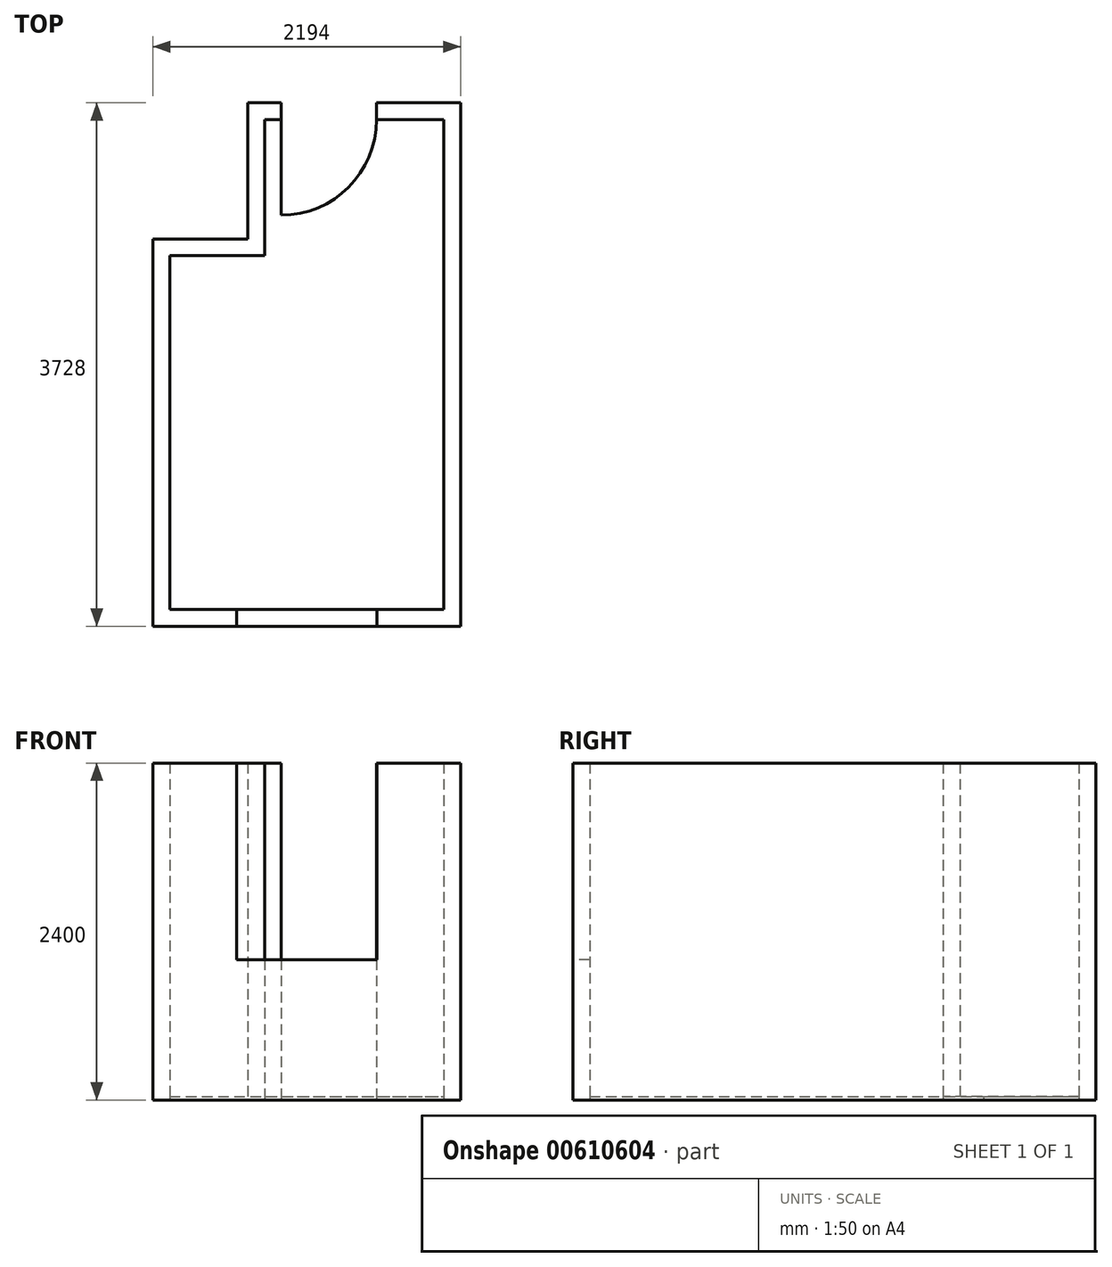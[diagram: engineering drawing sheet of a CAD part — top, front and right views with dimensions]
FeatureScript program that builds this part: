
annotation { "Feature Type Name" : "Feature", "Feature Type Description" : "" }
export const myFeature = defineFeature(function(context is Context, id is Id, definition is map)
    precondition{}
    {
        {
            var Q0;
            Q0=qCreatedBy(makeId("Top.planeOp"),FACE);
            var sketch = newSketch(context, id + "F0", { "sketchPlane" : qUnion([Q0])});
            skLineSegment(sketch, "E0.bottom", {"start": v(0, 0) * mm, "end": v(1954, 0) * mm});
            skLineSegment(sketch, "E0.top", {"start": v(677, 3488) * mm, "end": v(794, 3488) * mm});
            skLineSegment(sketch, "E0.left", {"start": v(0, 0) * mm, "end": v(0, 2519) * mm});
            skLineSegment(sketch, "E0.right", {"start": v(1954, 0) * mm, "end": v(1954, 3488) * mm});
            skLineSegment(sketch, "E1.top", {"start": v(0, 2519) * mm, "end": v(677, 2519) * mm});
            skLineSegment(sketch, "E1.right", {"start": v(677, 3488) * mm, "end": v(677, 2519) * mm});
            skLineSegment(sketch, "E2.bottom", {"start": v(2074, 3608) * mm, "end": v(1474, 3608) * mm});
            skLineSegment(sketch, "E2.top", {"start": v(2074, -120) * mm, "end": v(-120, -120) * mm});
            skLineSegment(sketch, "E2.left", {"start": v(2074, 3608) * mm, "end": v(2074, -120) * mm});
            skLineSegment(sketch, "E2.right", {"start": v(-120, 2519) * mm, "end": v(-120, -120) * mm});
            skPoint(sketch, "E2.middle", {"position": v(977, 1744) * mm});
            skPoint(sketch, "E2.middle.positionSnap0", {"position": v(977, 0) * mm});
            skPoint(sketch, "E2.middle.positionSnap1", {"position": v(0, 1744) * mm});
            skPoint(sketch, "E2.centerSnap0", {"position": v(977, 0) * mm});
            skPoint(sketch, "E2.centerSnap1", {"position": v(0, 1744) * mm});
            skLineSegment(sketch, "E3", {"start": v(1474, 3608) * mm, "end": v(1474, 3488) * mm});
            skLineSegment(sketch, "E4", {"start": v(794, 3608) * mm, "end": v(794, 3488) * mm});
            skArc(sketch, "E5", {"start": v(1474, 3488) * mm, "mid": v(1274.83, 3007.17) * mm, "end": v(794, 2808) * mm});
            skLineSegment(sketch, "E6", {"start": v(794, 2808) * mm, "end": v(794, 3488) * mm});
            skLineSegment(sketch, "E7.trimOffspring", {"start": v(1474, 3488) * mm, "end": v(1954, 3488) * mm});
            skLineSegment(sketch, "E8.trimOffspring", {"start": v(794, 3608) * mm, "end": v(677, 3608) * mm});
            skLineSegment(sketch, "E9", {"start": v(-120, 2519) * mm, "end": v(-120, 2639) * mm});
            skLineSegment(sketch, "E10", {"start": v(-120, 2639) * mm, "end": v(557, 2639) * mm});
            skLineSegment(sketch, "E11", {"start": v(557, 2639) * mm, "end": v(557, 3608) * mm});
            skLineSegment(sketch, "E12", {"start": v(557, 3608) * mm, "end": v(677, 3608) * mm});
            skLineSegment(sketch, "E13.bottom", {"start": v(398.12, 0) * mm, "end": v(1477, 0) * mm});
            skLineSegment(sketch, "E13.top", {"start": v(398.12, -120) * mm, "end": v(1477, -120) * mm});
            skLineSegment(sketch, "E13.right", {"start": v(1477, 0) * mm, "end": v(1477, -120) * mm});
            skLineSegment(sketch, "E14", {"start": v(477, 0) * mm, "end": v(477, -120) * mm});
            skSolve(sketch);
        }
        {
            var Q0;
            {var subQ3=sQuery(id+"F0.wireOp",EDGE,"E0.right");Q0=makeQuery(id+"F0.imprint","IMPRINT",FACE,{"disambiguationData":[TD([[makeQuery(id+"F0.imprint","IMPRINT",EDGE,{"derivedFrom":subQ3}),-1.0]])]});}
            var Q1;
            Q1=makeQuery(id+"F0.imprint","IMPRINT",FACE,{"disambiguationData":[TD([[makeQuery(id+"F0.imprint","IMPRINT",EDGE,{"derivedFrom":sQuery(id+"F0.wireOp",EDGE,"E0.top")}),1.0]])]});
            extrude(context, id + "F1", {"entities" : qUnion([Q0, Q1]), "depth" : 2400 * mm, "offsetDistance" : 25 * mm});
        }
        {
            var Q0;
            {var subQ0=sQuery(id+"F0.wireOp",EDGE,"E13.right");Q0=makeQuery(id+"F0.imprint","IMPRINT",FACE,{"disambiguationData":[TD([[makeQuery(id+"F0.imprint","IMPRINT",EDGE,{"derivedFrom":subQ0}),-1.0]])]});}
            extrude(context, id + "F2", {"entities" : qUnion([Q0]), "depth" : 1000 * mm, "offsetDistance" : 25 * mm});
        }
        {
            var Q0;
            {var subQ0=sQuery(id+"F0.wireOp",EDGE,"E13.right");Q0=makeQuery(id+"F0.imprint","IMPRINT",FACE,{"disambiguationData":[TD([[makeQuery(id+"F0.imprint","IMPRINT",EDGE,{"derivedFrom":subQ0}),-1.0]])]});}
            extrude(context, id + "F3", {"entities" : qUnion([Q0]), "operationType" : NewBodyOperationType.ADD, "depth" : 1000 * mm, "offsetDistance" : 25 * mm});
        }
        {
            var Q0;
            Q0=makeQuery(id+"F0.imprint","IMPRINT",FACE,{"disambiguationData":[TD([[makeQuery(id+"F0.imprint","IMPRINT",EDGE,{"derivedFrom":sQuery(id+"F0.wireOp",EDGE,"E0.top")}),-1.0]])]});
            extrude(context, id + "F4", {"entities" : qUnion([Q0]), "depth" : 25 * mm, "offsetDistance" : 25 * mm});
        }
    });
